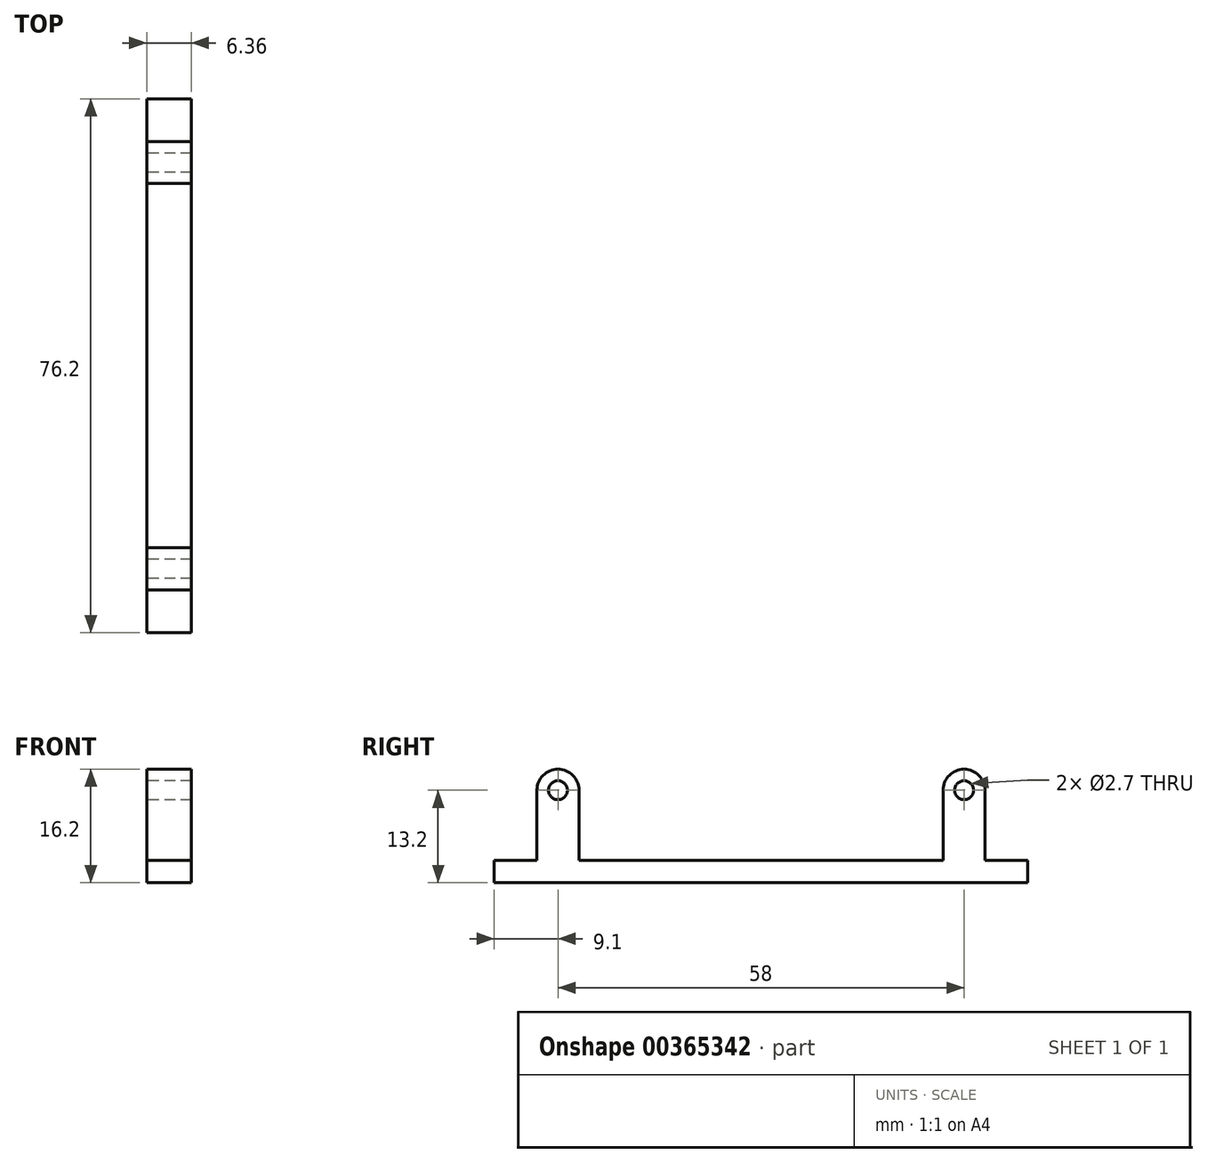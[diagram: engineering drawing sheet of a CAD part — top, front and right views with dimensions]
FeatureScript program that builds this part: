
annotation { "Feature Type Name" : "Feature", "Feature Type Description" : "" }
export const myFeature = defineFeature(function(context is Context, id is Id, definition is map)
    precondition{}
    {
        {
            var Q0;
            Q0=qCreatedBy(makeId("Right.planeOp"),FACE);
            var sketch = newSketch(context, id + "F0", { "sketchPlane" : qUnion([Q0])});
            skCircle(sketch, "E0", {"center": v(-29, 0) * mm, "radius": 1.35 * mm});
            skCircle(sketch, "E1", {"center": v(29, 0) * mm, "radius": 1.35 * mm});
            skLineSegment(sketch, "E2", {"start": v(-29, 0) * mm, "end": v(29, 0) * mm, "construction": true});
            skArc(sketch, "E3", {"start": v(-26, 0) * mm, "mid": v(-29, 3) * mm, "end": v(-32, 0) * mm});
            skArc(sketch, "E4", {"start": v(32, 0) * mm, "mid": v(29, 3) * mm, "end": v(26, 0) * mm});
            skLineSegment(sketch, "E5", {"start": v(-32, 0) * mm, "end": v(-32, -10) * mm});
            skLineSegment(sketch, "E6", {"start": v(-26, 0) * mm, "end": v(-26, -10) * mm});
            skLineSegment(sketch, "E7", {"start": v(26, 0) * mm, "end": v(26, -10) * mm});
            skLineSegment(sketch, "E8", {"start": v(32, 0) * mm, "end": v(32, -10) * mm});
            skLineSegment(sketch, "E9", {"start": v(-26, -10) * mm, "end": v(26, -10) * mm});
            skLineSegment(sketch, "E10", {"start": v(-32, -10) * mm, "end": v(-38.1, -10) * mm});
            skLineSegment(sketch, "E11", {"start": v(-38.1, -10) * mm, "end": v(-38.1, -13.2) * mm});
            skLineSegment(sketch, "E12", {"start": v(-38.1, -13.2) * mm, "end": v(38.1, -13.2) * mm});
            skLineSegment(sketch, "E13", {"start": v(38.1, -13.2) * mm, "end": v(38.1, -10) * mm});
            skLineSegment(sketch, "E14", {"start": v(38.1, -10) * mm, "end": v(32, -10) * mm});
            skLineSegment(sketch, "E15", {"start": v(0, 0) * mm, "end": v(0, -13.2) * mm, "construction": true});
            skSolve(sketch);
        }
        {
            var Q0;
            Q0=makeQuery(id+"F0.imprint","IMPRINT",FACE,{"disambiguationData":[TD([[makeQuery(id+"F0.imprint","IMPRINT",EDGE,{"derivedFrom":sQuery(id+"F0.wireOp",EDGE,"E0")}),-1.0]])]});
            extrude(context, id + "F1", {"entities" : qUnion([Q0]), "endBound" : BoundingType.SYMMETRIC, "depth" : 6.35 * mm});
        }
    });
